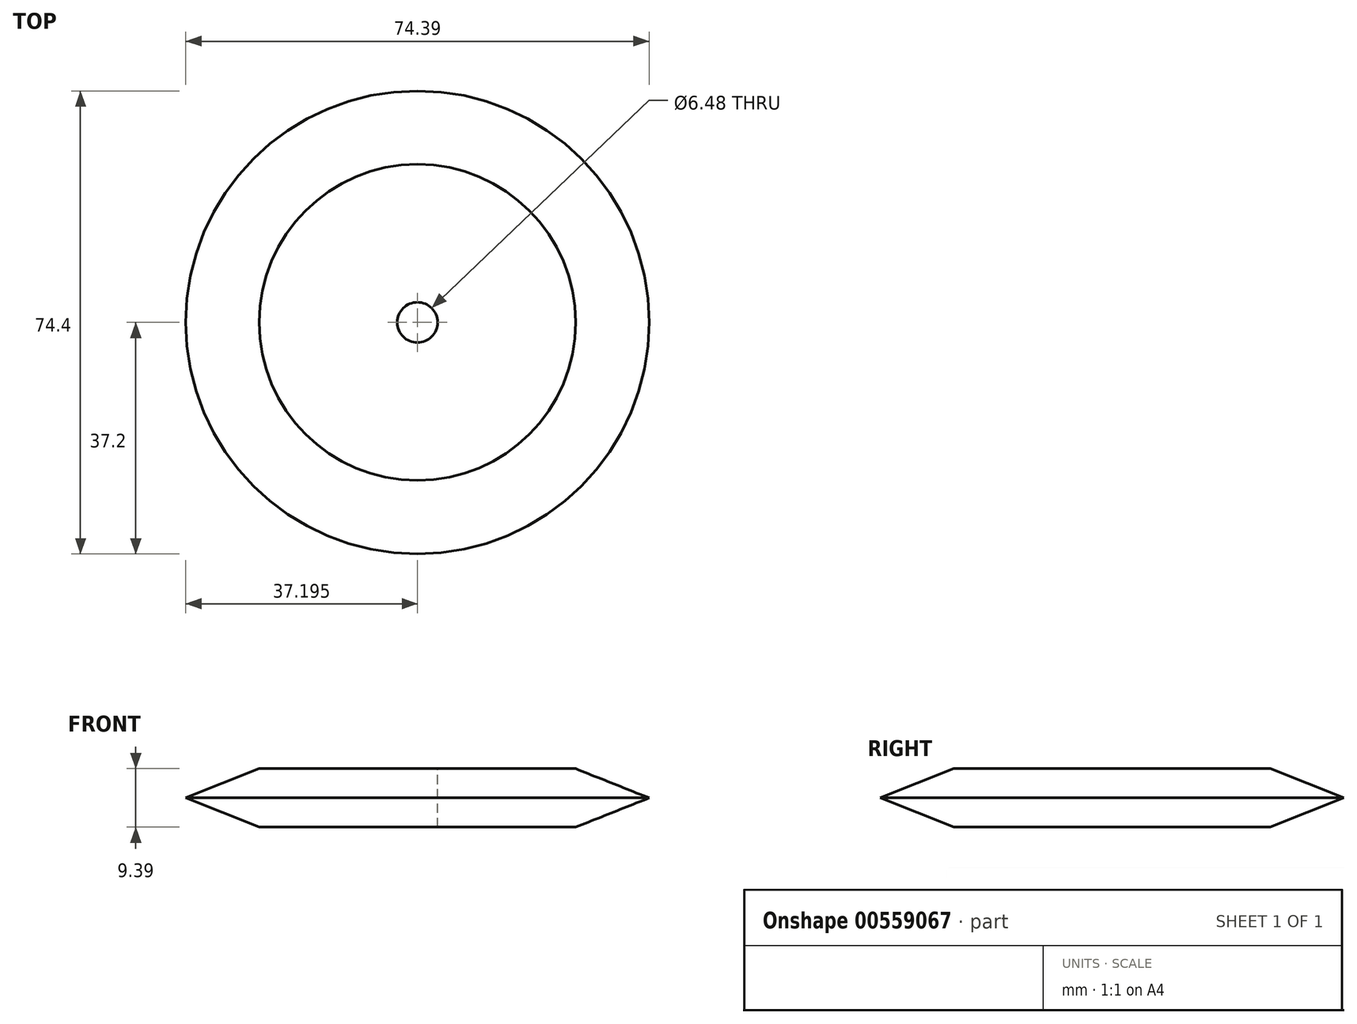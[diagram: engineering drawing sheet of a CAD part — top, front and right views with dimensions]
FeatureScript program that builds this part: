
annotation { "Feature Type Name" : "Feature", "Feature Type Description" : "" }
export const myFeature = defineFeature(function(context is Context, id is Id, definition is map)
    precondition{}
    {
        {
            var Q0;
            Q0=qCreatedBy(makeId("Front.planeOp"),FACE);
            var sketch = newSketch(context, id + "F0", { "sketchPlane" : qUnion([Q0])});
            skLineSegment(sketch, "E0.bottom", {"start": v(41.2, 20.83) * mm, "end": v(66.6, 20.83) * mm});
            skLineSegment(sketch, "E0.top", {"start": v(41.2, 11.44) * mm, "end": v(66.6, 11.44) * mm});
            skLineSegment(sketch, "E0.left", {"start": v(41.2, 20.83) * mm, "end": v(41.2, 11.44) * mm});
            skLineSegment(sketch, "E0.right", {"start": v(66.6, 20.83) * mm, "end": v(66.6, 11.44) * mm});
            skLineSegment(sketch, "E1", {"start": v(66.6, 20.83) * mm, "end": v(78.4, 16.13) * mm});
            skPoint(sketch, "E1.endSnap0", {"position": v(66.6, 16.13) * mm});
            skLineSegment(sketch, "E2", {"start": v(78.4, 16.13) * mm, "end": v(66.6, 11.44) * mm});
            skSolve(sketch);
        }
        {
            var Q0;
            Q0=makeQuery(id+"F0.imprint","IMPRINT",FACE,{"disambiguationData":[TD([[makeQuery(id+"F0.imprint","IMPRINT",EDGE,{"derivedFrom":sQuery(id+"F0.wireOp",EDGE,"E0.bottom")}),-1.0]])]});
            var Q1;
            Q1=makeQuery(id+"F0.imprint","IMPRINT",FACE,{"disambiguationData":[TD([[makeQuery(id+"F0.imprint","IMPRINT",EDGE,{"derivedFrom":sQuery(id+"F0.wireOp",EDGE,"E0.right")}),1.0]])]});
            var Q2;
            Q2=sQuery(id+"F0.wireOp",EDGE,"E0.left");
            revolve(context, id + "F1", {"entities" : qUnion([Q0, Q1]), "axis" : qUnion([Q2]), "revolveType" : RevolveType.FULL});
        }
        {
            var Q0;
            Q0=makeQuery(id+"F1.opRevolve","SWEPT_FACE",FACE,{"disambiguationData":[OSD([sQuery(id+"F0.wireOp",EDGE,"E0.bottom")])]});
            var sketch = newSketch(context, id + "F2", { "sketchPlane" : qUnion([Q0])});
            skCircle(sketch, "E3", {"center": v(41.2, 0) * mm, "radius": 3.24 * mm});
            skSolve(sketch);
        }
        {
            var Q0;
            Q0=makeQuery(id+"F2.imprint","IMPRINT",FACE,{"disambiguationData":[TD([[makeQuery(id+"F2.imprint","IMPRINT",EDGE,{"derivedFrom":sQuery(id+"F2.wireOp",EDGE,"E3")}),1.0]])]});
            extrude(context, id + "F3", {"entities" : qUnion([Q0]), "operationType" : NewBodyOperationType.REMOVE, "oppositeDirection" : true, "depth" : 47 * mm, "offsetDistance" : 25.4 * mm});
        }
    });
